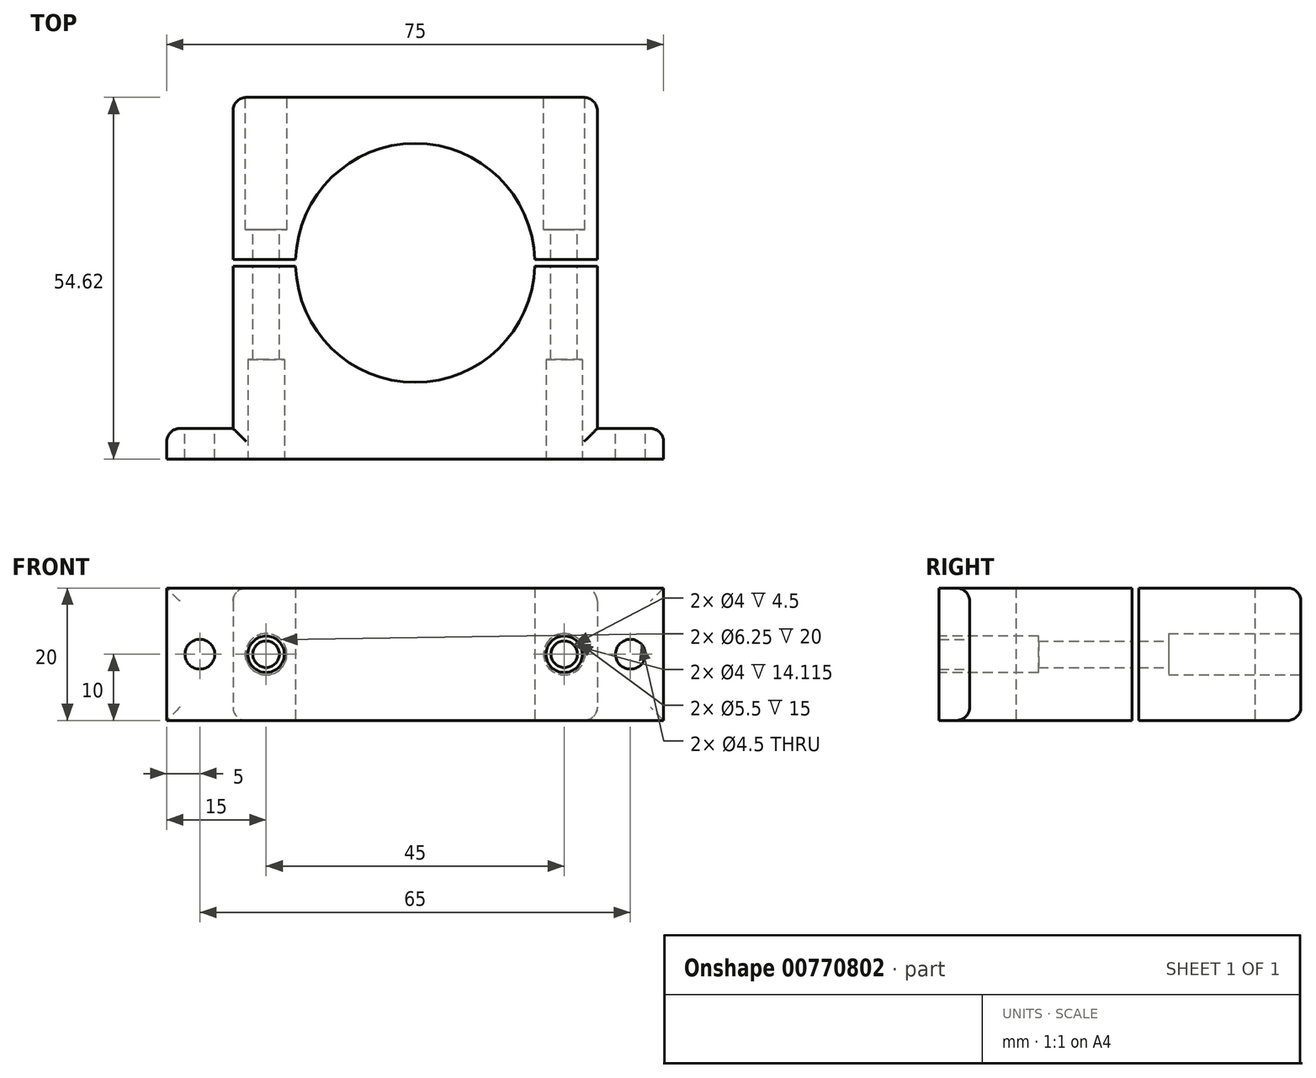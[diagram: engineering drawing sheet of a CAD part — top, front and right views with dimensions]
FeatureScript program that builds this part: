
annotation { "Feature Type Name" : "Feature", "Feature Type Description" : "" }
export const myFeature = defineFeature(function(context is Context, id is Id, definition is map)
    precondition{}
    {
        {
            var Q0;
            Q0=qCreatedBy(makeId("Top.planeOp"),FACE);
            var sketch = newSketch(context, id + "F0", { "sketchPlane" : qUnion([Q0])});
            skCircle(sketch, "E0", {"center": v(0, 0) * mm, "radius": 18.05 * mm});
            skLineSegment(sketch, "E1.top", {"start": v(27.5, 25) * mm, "end": v(-27.5, 25) * mm});
            skLineSegment(sketch, "E1.left", {"start": v(27.5, -25) * mm, "end": v(27.5, 25) * mm});
            skLineSegment(sketch, "E1.right", {"start": v(-27.5, -25) * mm, "end": v(-27.5, 25) * mm});
            skLineSegment(sketch, "E2.bottom", {"start": v(37.5, -29.62) * mm, "end": v(-37.5, -29.62) * mm});
            skLineSegment(sketch, "E2.left", {"start": v(37.5, -29.62) * mm, "end": v(37.5, -25) * mm});
            skLineSegment(sketch, "E2.right", {"start": v(-37.5, -29.62) * mm, "end": v(-37.5, -25) * mm});
            skPoint(sketch, "E2.middle", {"position": v(0, -25) * mm});
            skLineSegment(sketch, "E3", {"start": v(27.5, -25) * mm, "end": v(37.5, -25) * mm});
            skLineSegment(sketch, "E4", {"start": v(-27.5, -25) * mm, "end": v(-37.5, -25) * mm});
            skPoint(sketch, "E5.orphan", {"position": v(37.5, -20.38) * mm});
            skPoint(sketch, "E6.orphan", {"position": v(-37.5, -20.38) * mm});
            skLineSegment(sketch, "E7", {"start": v(-27.5, 0) * mm, "end": v(27.5, 0) * mm});
            skSolve(sketch);
        }
        {
            var Q0;
            Q0=makeQuery(id+"F0.imprint","IMPRINT",FACE,{"disambiguationData":[TD([[makeQuery(id+"F0.imprint","IMPRINT",EDGE,{"derivedFrom":sQuery(id+"F0.wireOp",EDGE,"E2.bottom")}),-1.0]])]});
            extrude(context, id + "F1", {"entities" : qUnion([Q0]), "depth" : 20 * mm, "offsetDistance" : 25 * mm});
        }
        {
            var Q0;
            {var subQ1=sQuery(id+"F0.wireOp",EDGE,"E1.top");Q0=makeQuery(id+"F0.imprint","IMPRINT",FACE,{"disambiguationData":[TD([[makeQuery(id+"F0.imprint","IMPRINT",EDGE,{"derivedFrom":subQ1}),1.0]])]});}
            extrude(context, id + "F2", {"entities" : qUnion([Q0]), "depth" : 20 * mm, "offsetDistance" : 25 * mm});
        }
        {
            var Q0;
            Q0=makeQuery(id+"F1.opExtrude","SWEPT_FACE",FACE,{"disambiguationData":[OSD([sQuery(id+"F0.wireOp",EDGE,"E3")])]});
            var sketch = newSketch(context, id + "F3", { "sketchPlane" : qUnion([Q0])});
            skCircle(sketch, "E8", {"center": v(-32.5, 10) * mm, "radius": 2.25 * mm});
            skCircle(sketch, "E9", {"center": v(32.5, 10) * mm, "radius": 2.25 * mm});
            skPoint(sketch, "E9.centerSnap0", {"position": v(-27.5, 10) * mm});
            skSolve(sketch);
        }
        {
            var Q0;
            Q0=makeQuery(id+"F2.opExtrude","SWEPT_FACE",FACE,{"disambiguationData":[OSD([sQuery(id+"F0.wireOp",EDGE,"E1.top")])]});
            var sketch = newSketch(context, id + "F4", { "sketchPlane" : qUnion([Q0])});
            skCircle(sketch, "E10", {"center": v(-22.5, 10) * mm, "radius": 2 * mm});
            skPoint(sketch, "E10.centerSnap0", {"position": v(-27.5, 10) * mm});
            skCircle(sketch, "E11", {"center": v(22.5, 10) * mm, "radius": 2 * mm});
            skSolve(sketch);
        }
        {
            var Q0;
            Q0=makeQuery(id+"F4.imprint","IMPRINT",FACE,{"disambiguationData":[TD([[makeQuery(id+"F4.imprint","IMPRINT",EDGE,{"derivedFrom":sQuery(id+"F4.wireOp",EDGE,"E10")}),1.0]])]});
            var Q1;
            Q1=makeQuery(id+"F4.imprint","IMPRINT",FACE,{"disambiguationData":[TD([[makeQuery(id+"F4.imprint","IMPRINT",EDGE,{"derivedFrom":sQuery(id+"F4.wireOp",EDGE,"E11")}),1.0]])]});
            extrude(context, id + "F5", {"entities" : qUnion([Q0, Q1]), "operationType" : NewBodyOperationType.REMOVE, "endBound" : BoundingType.THROUGH_ALL, "oppositeDirection" : true, "depth" : 25 * mm, "offsetDistance" : 25 * mm});
        }
        {
            var Q0;
            Q0=makeQuery(id+"F1.opExtrude","SWEPT_FACE",FACE,{"disambiguationData":[OSD([sQuery(id+"F0.wireOp",EDGE,"E2.bottom")])]});
            var sketch = newSketch(context, id + "F6", { "sketchPlane" : qUnion([Q0])});
            skCircle(sketch, "E12.0", {"center": v(22.5, 10) * mm, "radius": 2 * mm, "construction": true});
            skCircle(sketch, "E12.1", {"center": v(-22.5, 10) * mm, "radius": 2 * mm, "construction": true});
            skCircle(sketch, "E13", {"center": v(22.5, 10) * mm, "radius": 2.75 * mm});
            skCircle(sketch, "E14", {"center": v(-22.5, 10) * mm, "radius": 2.75 * mm});
            skSolve(sketch);
        }
        {
            var Q0;
            Q0=makeQuery(id+"F6.imprint","IMPRINT",FACE,{"disambiguationData":[TD([[makeQuery(id+"F6.imprint","IMPRINT",EDGE,{"derivedFrom":sQuery(id+"F6.wireOp",EDGE,"E13")}),1.0]])]});
            var Q1;
            Q1=makeQuery(id+"F6.imprint","IMPRINT",FACE,{"disambiguationData":[TD([[makeQuery(id+"F6.imprint","IMPRINT",EDGE,{"derivedFrom":sQuery(id+"F6.wireOp",EDGE,"E14")}),1.0]])]});
            extrude(context, id + "F7", {"entities" : qUnion([Q0, Q1]), "operationType" : NewBodyOperationType.REMOVE, "oppositeDirection" : true, "depth" : 15 * mm, "offsetDistance" : 25 * mm});
        }
        {
            var Q0;
            Q0=makeQuery(id+"F2.opExtrude","SWEPT_FACE",FACE,{"disambiguationData":[OSD([sQuery(id+"F0.wireOp",EDGE,"E1.top")])]});
            var sketch = newSketch(context, id + "F8", { "sketchPlane" : qUnion([Q0])});
            skCircle(sketch, "E15.0", {"center": v(-22.5, 10) * mm, "radius": 2 * mm, "construction": true});
            skCircle(sketch, "E15.1", {"center": v(22.5, 10) * mm, "radius": 2 * mm, "construction": true});
            skCircle(sketch, "E16", {"center": v(-22.5, 10) * mm, "radius": 3.12 * mm});
            skCircle(sketch, "E17", {"center": v(22.5, 10) * mm, "radius": 3.12 * mm});
            skSolve(sketch);
        }
        {
            var Q0;
            Q0=makeQuery(id+"F8.imprint","IMPRINT",FACE,{"disambiguationData":[TD([[makeQuery(id+"F8.imprint","IMPRINT",EDGE,{"derivedFrom":sQuery(id+"F8.wireOp",EDGE,"E16")}),1.0]])]});
            var Q1;
            Q1=makeQuery(id+"F8.imprint","IMPRINT",FACE,{"disambiguationData":[TD([[makeQuery(id+"F8.imprint","IMPRINT",EDGE,{"derivedFrom":sQuery(id+"F8.wireOp",EDGE,"E17")}),1.0]])]});
            extrude(context, id + "F9", {"entities" : qUnion([Q0, Q1]), "operationType" : NewBodyOperationType.REMOVE, "oppositeDirection" : true, "depth" : 20 * mm, "offsetDistance" : 25 * mm});
        }
        {
            var Q0;
            Q0=makeQuery(id+"F3.imprint","IMPRINT",FACE,{"disambiguationData":[TD([[makeQuery(id+"F3.imprint","IMPRINT",EDGE,{"derivedFrom":sQuery(id+"F3.wireOp",EDGE,"E8")}),1.0]])]});
            var Q1;
            Q1=makeQuery(id+"F3.imprint","IMPRINT",FACE,{"disambiguationData":[TD([[makeQuery(id+"F3.imprint","IMPRINT",EDGE,{"derivedFrom":sQuery(id+"F3.wireOp",EDGE,"E9")}),1.0]])]});
            extrude(context, id + "F10", {"entities" : qUnion([Q0, Q1]), "operationType" : NewBodyOperationType.REMOVE, "endBound" : BoundingType.THROUGH_ALL, "oppositeDirection" : true, "depth" : 25 * mm, "offsetDistance" : 25 * mm});
        }
        {
            var Q0;
            Q0=makeQuery(id+"F0.imprint","IMPRINT",FACE,{"disambiguationData":[TD([[makeQuery(id+"F0.imprint","IMPRINT",EDGE,{"derivedFrom":sQuery(id+"F0.wireOp",EDGE,"E2.bottom")}),-1.0]])]});
            var sketch = newSketch(context, id + "F11", { "sketchPlane" : qUnion([Q0])});
            skLineSegment(sketch, "E18.0", {"start": v(20.5, 5) * mm, "end": v(24.5, 5) * mm});
            skLineSegment(sketch, "E18.1", {"start": v(20.5, 0) * mm, "end": v(24.5, 0) * mm});
            skLineSegment(sketch, "E19.0", {"start": v(24.5, -14.62) * mm, "end": v(20.5, -14.62) * mm});
            skLineSegment(sketch, "E20.bottom", {"start": v(-27.5, -0.5) * mm, "end": v(27.5, -0.5) * mm});
            skLineSegment(sketch, "E20.top", {"start": v(-27.5, 0.5) * mm, "end": v(27.5, 0.5) * mm});
            skLineSegment(sketch, "E20.left", {"start": v(-27.5, -0.5) * mm, "end": v(-27.5, 0.5) * mm});
            skLineSegment(sketch, "E20.right", {"start": v(27.5, -0.5) * mm, "end": v(27.5, 0.5) * mm});
            skPoint(sketch, "E20.middle", {"position": v(0, 0) * mm});
            skSolve(sketch);
        }
        {
            var Q0;
            {var subQ11=sQuery(id+"F11.wireOp",EDGE,"E18.1");Q0=makeQuery(id+"F11.imprint","IMPRINT",FACE,{"disambiguationData":[TD([[makeQuery(id+"F11.imprint","IMPRINT",EDGE,{"derivedFrom":subQ11}),1.0]])]});}
            var Q1;
            {var subQ13=sQuery(id+"F11.wireOp",EDGE,"E18.1");Q1=makeQuery(id+"F11.imprint","IMPRINT",FACE,{"disambiguationData":[TD([[makeQuery(id+"F11.imprint","IMPRINT",EDGE,{"derivedFrom":subQ13}),-1.0]])]});}
            var Q2;
            {var subQ2=sQuery(id+"F0.wireOp",EDGE,"E1.right");var subQ3=sQuery(id+"F0.wireOp",EDGE,"E7");var subQ4=makeQuery(id+"F0.imprint","INTERSECT",VERTEX,{"derivedFrom":[subQ2,subQ3]});var subQ10=makeQuery(id+"F0.imprint","IMPRINT",EDGE,{"disambiguationData":[TD([[subQ4,-1.0]])],"derivedFrom":subQ3});Q2=makeQuery(id+"F11.imprint","IMPRINT",FACE,{"disambiguationData":[TD([[makeQuery(id+"F11.imprint","IMPRINT",EDGE,{"derivedFrom":subQ10}),-1.0]])]});}
            extrude(context, id + "F12", {"entities" : qUnion([Q0, Q1, Q2]), "operationType" : NewBodyOperationType.REMOVE, "endBound" : BoundingType.THROUGH_ALL, "depth" : 25 * mm, "offsetDistance" : 25 * mm});
        }
        {
            var Q0;
            Q0=makeQuery(id+"F2.opExtrude","SWEPT_EDGE",EDGE,{"disambiguationData":[OSD([sQuery(id+"F0.wireOp",EDGE,"E1.top"),sQuery(id+"F0.wireOp",EDGE,"E1.left")])]});
            var Q1;
            Q1=makeQuery(id+"F2.opExtrude","CAP_EDGE",EDGE,{"disambiguationData":[OSD([sQuery(id+"F0.wireOp",EDGE,"E1.top")])],"isStart":false});
            var Q2;
            Q2=makeQuery(id+"F2.opExtrude","CAP_EDGE",EDGE,{"disambiguationData":[OSD([sQuery(id+"F0.wireOp",EDGE,"E1.top")])],"isStart":true});
            var Q3;
            Q3=makeQuery(id+"F2.opExtrude","SWEPT_EDGE",EDGE,{"disambiguationData":[OSD([sQuery(id+"F0.wireOp",EDGE,"E1.top"),sQuery(id+"F0.wireOp",EDGE,"E1.right")])]});
            var Q4;
            Q4=makeQuery(id+"F2.opExtrude","CAP_EDGE",EDGE,{"disambiguationData":[OSD([sQuery(id+"F0.wireOp",EDGE,"E1.right")])],"isStart":true});
            var Q5;
            Q5=makeQuery(id+"F2.opExtrude","CAP_EDGE",EDGE,{"disambiguationData":[OSD([sQuery(id+"F0.wireOp",EDGE,"E1.right")])],"isStart":false});
            var Q6;
            Q6=makeQuery(id+"F1.opExtrude","CAP_EDGE",EDGE,{"disambiguationData":[OSD([sQuery(id+"F0.wireOp",EDGE,"E1.right")])],"isStart":true});
            var Q7;
            Q7=makeQuery(id+"F1.opExtrude","CAP_EDGE",EDGE,{"disambiguationData":[OSD([sQuery(id+"F0.wireOp",EDGE,"E1.right")])],"isStart":false});
            var Q8;
            Q8=makeQuery(id+"F1.opExtrude","CAP_EDGE",EDGE,{"disambiguationData":[OSD([sQuery(id+"F0.wireOp",EDGE,"E4")])],"isStart":true});
            var Q9;
            Q9=makeQuery(id+"F1.opExtrude","SWEPT_EDGE",EDGE,{"disambiguationData":[OSD([sQuery(id+"F0.wireOp",EDGE,"E2.right"),sQuery(id+"F0.wireOp",EDGE,"E4")])]});
            var Q10;
            Q10=makeQuery(id+"F1.opExtrude","CAP_EDGE",EDGE,{"disambiguationData":[OSD([sQuery(id+"F0.wireOp",EDGE,"E4")])],"isStart":false});
            var Q11;
            Q11=makeQuery(id+"F2.opExtrude","CAP_EDGE",EDGE,{"disambiguationData":[OSD([sQuery(id+"F0.wireOp",EDGE,"E1.left")])],"isStart":false});
            var Q12;
            Q12=makeQuery(id+"F2.opExtrude","CAP_EDGE",EDGE,{"disambiguationData":[OSD([sQuery(id+"F0.wireOp",EDGE,"E1.left")])],"isStart":true});
            var Q13;
            Q13=makeQuery(id+"F1.opExtrude","CAP_EDGE",EDGE,{"disambiguationData":[OSD([sQuery(id+"F0.wireOp",EDGE,"E1.left")])],"isStart":true});
            var Q14;
            Q14=makeQuery(id+"F1.opExtrude","CAP_EDGE",EDGE,{"disambiguationData":[OSD([sQuery(id+"F0.wireOp",EDGE,"E1.left")])],"isStart":false});
            var Q15;
            Q15=makeQuery(id+"F1.opExtrude","SWEPT_EDGE",EDGE,{"disambiguationData":[OSD([sQuery(id+"F0.wireOp",EDGE,"E2.left"),sQuery(id+"F0.wireOp",EDGE,"E3")])]});
            var Q16;
            Q16=makeQuery(id+"F1.opExtrude","CAP_EDGE",EDGE,{"disambiguationData":[OSD([sQuery(id+"F0.wireOp",EDGE,"E3")])],"isStart":false});
            var Q17;
            Q17=makeQuery(id+"F1.opExtrude","CAP_EDGE",EDGE,{"disambiguationData":[OSD([sQuery(id+"F0.wireOp",EDGE,"E3")])],"isStart":true});
            fillet(context, id + "F13", {"entities" : qUnion([Q0, Q1, Q2, Q3, Q4, Q5, Q6, Q7, Q8, Q9, Q10, Q11, Q12, Q13, Q14, Q15, Q16, Q17]), "radius" : 2 * mm, "tangentPropagation" : true, "allowEdgeOverflow" : false});
        }
    });
